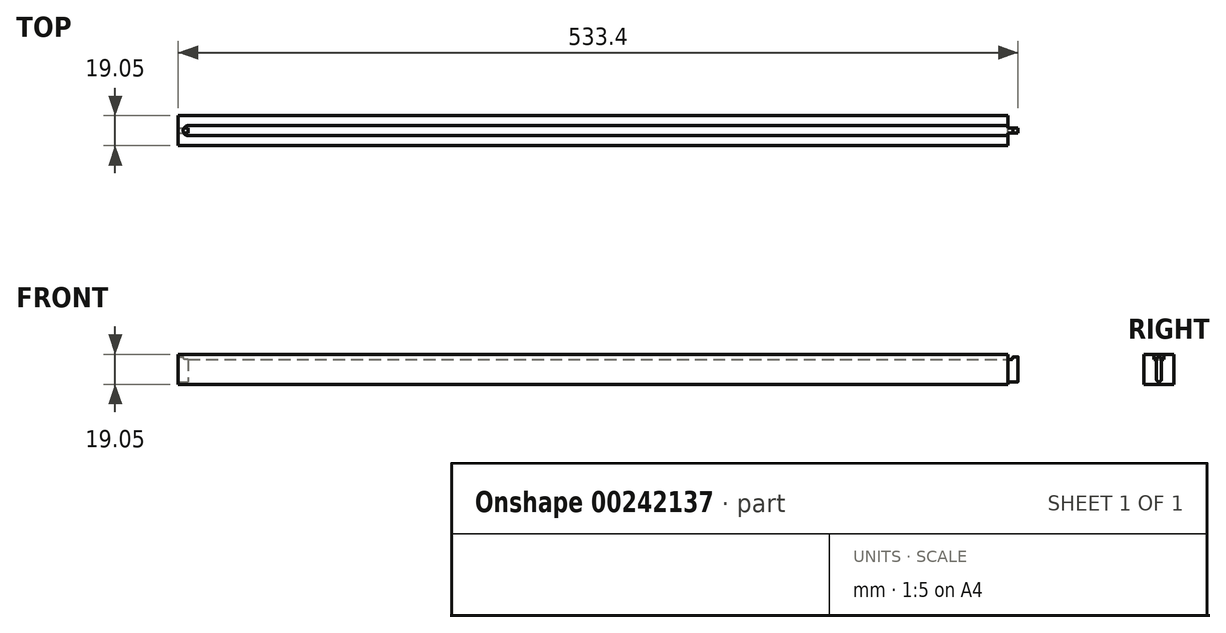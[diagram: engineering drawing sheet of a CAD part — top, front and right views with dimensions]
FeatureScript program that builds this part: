
annotation { "Feature Type Name" : "Feature", "Feature Type Description" : "" }
export const myFeature = defineFeature(function(context is Context, id is Id, definition is map)
    precondition{}
    {
        {
            var Q0;
            Q0=qCreatedBy(makeId("Right.planeOp"),FACE);
            var sketch = newSketch(context, id + "F0", { "sketchPlane" : qUnion([Q0])});
            skLineSegment(sketch, "E0.bottom", {"start": v(0, 0) * mm, "end": v(-19.05, 0) * mm});
            skLineSegment(sketch, "E0.top", {"start": v(0, 19.05) * mm, "end": v(-19.05, 19.05) * mm});
            skLineSegment(sketch, "E0.left", {"start": v(0, 0) * mm, "end": v(0, 19.05) * mm});
            skLineSegment(sketch, "E0.right", {"start": v(-19.05, 0) * mm, "end": v(-19.05, 19.05) * mm});
            skSolve(sketch);
        }
        {
            var Q0;
            Q0 = qSketchRegion(id + "F0", true);
            extrude(context, id + "F1", {"entities" : qUnion([Q0]), "depth" : 520.7 * mm});
        }
        {
            var Q0;
            Q0=makeQuery(id+"F1.opExtrude","CAP_FACE",FACE,{"disambiguationData":[OSD([sQuery(id+"F0.wireOp",EDGE,"E0.bottom"),sQuery(id+"F0.wireOp",EDGE,"E0.top"),sQuery(id+"F0.wireOp",EDGE,"E0.left"),sQuery(id+"F0.wireOp",EDGE,"E0.right")])],"isStart":false});
            var sketch = newSketch(context, id + "F2", { "sketchPlane" : qUnion([Q0])});
            skLineSegment(sketch, "E1", {"start": v(-9.53, 15.88) * mm, "end": v(-9.53, 3.18) * mm});
            skPoint(sketch, "E1.startSnap0", {"position": v(-9.53, 19.05) * mm});
            skArc(sketch, "E2.0.startCap", {"start": v(-11.11, 15.88) * mm, "mid": v(-9.53, 17.46) * mm, "end": v(-7.94, 15.88) * mm});
            skArc(sketch, "E2.0.endCap", {"start": v(-7.94, 3.18) * mm, "mid": v(-9.53, 1.59) * mm, "end": v(-11.11, 3.18) * mm});
            skLineSegment(sketch, "E2.0.left", {"start": v(-7.94, 15.88) * mm, "end": v(-7.94, 3.18) * mm});
            skLineSegment(sketch, "E2.0.right", {"start": v(-11.11, 15.88) * mm, "end": v(-11.11, 3.18) * mm});
            skSolve(sketch);
        }
        {
            var Q0;
            Q0 = qSketchRegion(id + "F2", true);
            extrude(context, id + "F3", {"entities" : qUnion([Q0]), "operationType" : NewBodyOperationType.ADD, "depth" : 6.35 * mm});
        }
        {
            var Q0;
            Q0=makeQuery(id+"F1.opExtrude","CAP_FACE",FACE,{"disambiguationData":[OSD([sQuery(id+"F0.wireOp",EDGE,"E0.bottom"),sQuery(id+"F0.wireOp",EDGE,"E0.top"),sQuery(id+"F0.wireOp",EDGE,"E0.left"),sQuery(id+"F0.wireOp",EDGE,"E0.right")])],"isStart":true});
            var sketch = newSketch(context, id + "F4", { "sketchPlane" : qUnion([Q0])});
            skLineSegment(sketch, "E3", {"start": v(9.53, 15.88) * mm, "end": v(9.53, 3.18) * mm});
            skPoint(sketch, "E3.startSnap0", {"position": v(9.53, 19.05) * mm});
            skArc(sketch, "E4.0.startCap", {"start": v(7.94, 15.88) * mm, "mid": v(9.53, 17.46) * mm, "end": v(11.11, 15.88) * mm});
            skArc(sketch, "E4.0.endCap", {"start": v(11.11, 3.18) * mm, "mid": v(9.53, 1.59) * mm, "end": v(7.94, 3.18) * mm});
            skLineSegment(sketch, "E4.0.left", {"start": v(11.11, 15.88) * mm, "end": v(11.11, 3.18) * mm});
            skLineSegment(sketch, "E4.0.right", {"start": v(7.94, 15.88) * mm, "end": v(7.94, 3.18) * mm});
            skSolve(sketch);
        }
        {
            var Q0;
            Q0=makeQuery(id+"F4.imprint","IMPRINT",FACE,{"disambiguationData":[TD([[makeQuery(id+"F4.imprint","IMPRINT",EDGE,{"derivedFrom":sQuery(id+"F4.wireOp",EDGE,"E4.0.startCap")}),-1.0]])]});
            extrude(context, id + "F5", {"entities" : qUnion([Q0]), "operationType" : NewBodyOperationType.ADD, "depth" : 6.35 * mm});
        }
        {
            var Q0;
            Q0=makeQuery(id+"F1.opExtrude","SWEPT_FACE",FACE,{"disambiguationData":[OSD([sQuery(id+"F0.wireOp",EDGE,"E0.top")])]});
            var sketch = newSketch(context, id + "F6", { "sketchPlane" : qUnion([Q0])});
            skLineSegment(sketch, "E5", {"start": v(0, -9.53) * mm, "end": v(520.7, -9.53) * mm});
            skArc(sketch, "E6.0.startCap", {"start": v(0, -12.7) * mm, "mid": v(-3.18, -9.53) * mm, "end": v(0, -6.35) * mm});
            skArc(sketch, "E6.0.endCap", {"start": v(520.7, -6.35) * mm, "mid": v(523.88, -9.53) * mm, "end": v(520.7, -12.7) * mm});
            skLineSegment(sketch, "E6.0.left", {"start": v(0, -6.35) * mm, "end": v(520.7, -6.35) * mm});
            skLineSegment(sketch, "E6.0.right", {"start": v(0, -12.7) * mm, "end": v(520.7, -12.7) * mm});
            skSolve(sketch);
        }
        {
            var Q0;
            Q0 = qSketchRegion(id + "F6", true);
            extrude(context, id + "F7", {"entities" : qUnion([Q0]), "operationType" : NewBodyOperationType.REMOVE, "oppositeDirection" : true, "depth" : 3.17 * mm});
        }
    });
